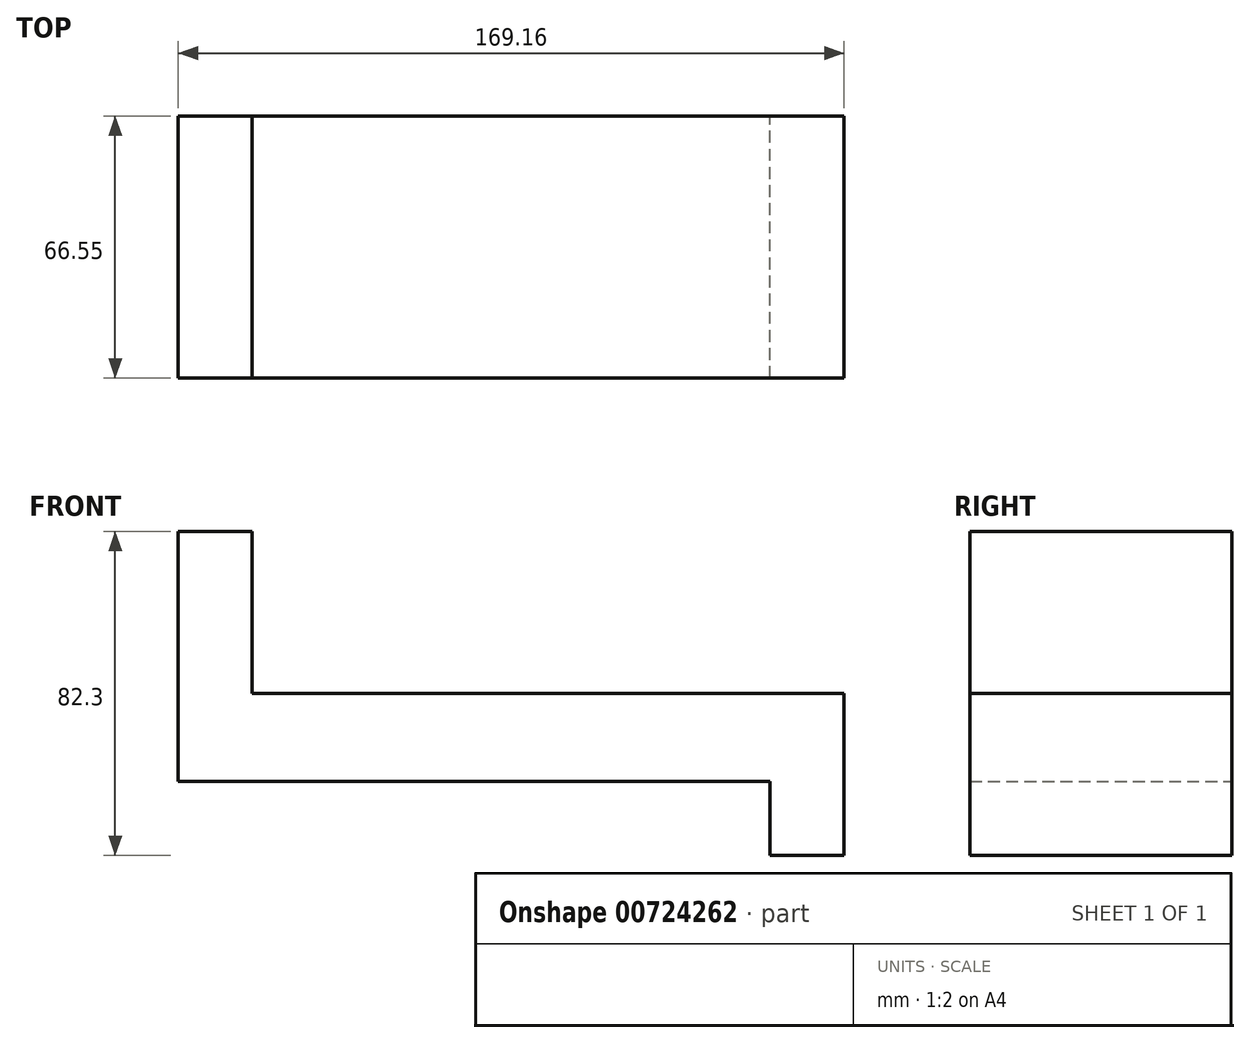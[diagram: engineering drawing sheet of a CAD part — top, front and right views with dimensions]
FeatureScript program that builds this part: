
annotation { "Feature Type Name" : "Feature", "Feature Type Description" : "" }
export const myFeature = defineFeature(function(context is Context, id is Id, definition is map)
    precondition{}
    {
        {
            var Q0;
            Q0=qCreatedBy(makeId("Front.planeOp"),FACE);
            var sketch = newSketch(context, id + "F0", { "sketchPlane" : qUnion([Q0])});
            skLineSegment(sketch, "E0", {"start": v(-108.48, 54.68) * mm, "end": v(-108.48, -8.82) * mm});
            skLineSegment(sketch, "E1", {"start": v(-108.48, -8.82) * mm, "end": v(41.89, -8.82) * mm});
            skLineSegment(sketch, "E2", {"start": v(41.89, -8.82) * mm, "end": v(41.89, -27.62) * mm});
            skLineSegment(sketch, "E3", {"start": v(41.89, -27.62) * mm, "end": v(60.68, -27.62) * mm});
            skLineSegment(sketch, "E4", {"start": v(60.68, -27.62) * mm, "end": v(60.68, 13.53) * mm});
            skLineSegment(sketch, "E5", {"start": v(60.68, 13.53) * mm, "end": v(-89.69, 13.53) * mm});
            skLineSegment(sketch, "E6", {"start": v(-89.69, 13.53) * mm, "end": v(-89.69, 54.68) * mm});
            skLineSegment(sketch, "E7", {"start": v(-108.48, 54.68) * mm, "end": v(-89.69, 54.68) * mm});
            skSolve(sketch);
        }
        {
            var Q0;
            Q0 = qSketchRegion(id + "F0", true);
            extrude(context, id + "F1", {"entities" : qUnion([Q0]), "depth" : 66.55 * mm, "offsetDistance" : 25.4 * mm});
        }
    });
